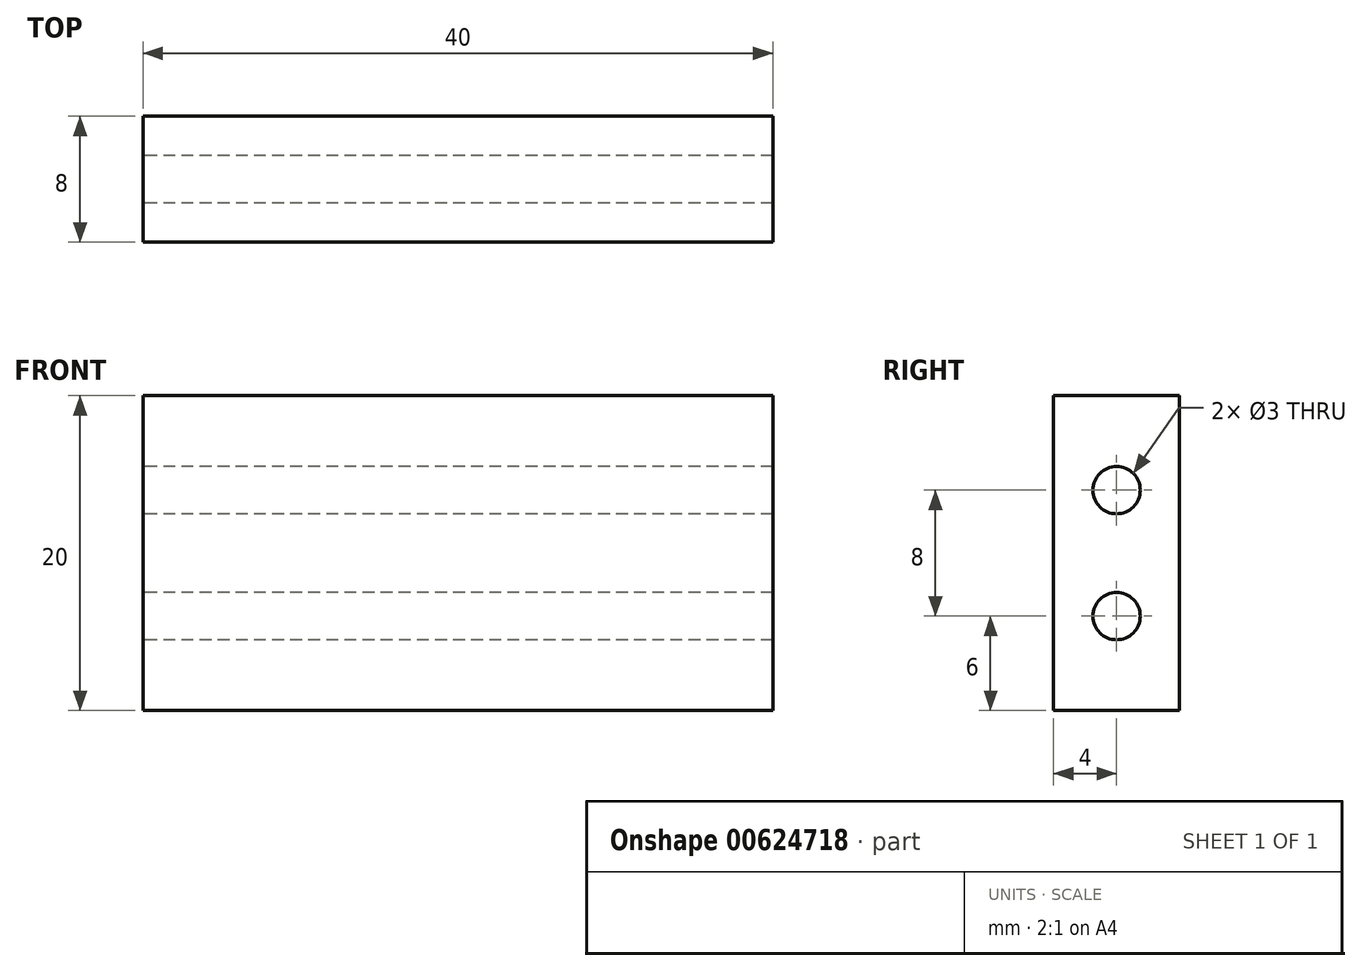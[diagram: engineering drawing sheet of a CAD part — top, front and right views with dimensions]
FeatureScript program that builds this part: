
annotation { "Feature Type Name" : "Feature", "Feature Type Description" : "" }
export const myFeature = defineFeature(function(context is Context, id is Id, definition is map)
    precondition{}
    {
        {
            var Q0;
            Q0=qCreatedBy(makeId("Front.planeOp"),FACE);
            var sketch = newSketch(context, id + "F0", { "sketchPlane" : qUnion([Q0])});
            skLineSegment(sketch, "E0.bottom", {"start": v(-20, -10) * mm, "end": v(20, -10) * mm});
            skLineSegment(sketch, "E0.top", {"start": v(-20, 10) * mm, "end": v(20, 10) * mm});
            skLineSegment(sketch, "E0.left", {"start": v(-20, -10) * mm, "end": v(-20, 10) * mm});
            skLineSegment(sketch, "E0.right", {"start": v(20, -10) * mm, "end": v(20, 10) * mm});
            skPoint(sketch, "E0.middle", {"position": v(0, 0) * mm});
            skSolve(sketch);
        }
        {
            var Q0;
            Q0=makeQuery(id+"F0.imprint","IMPRINT",FACE,{"disambiguationData":[TD([[makeQuery(id+"F0.imprint","IMPRINT",EDGE,{"derivedFrom":sQuery(id+"F0.wireOp",EDGE,"E0.bottom")}),1.0]])]});
            extrude(context, id + "F1", {"entities" : qUnion([Q0]), "depth" : 8 * mm, "offsetDistance" : 25 * mm});
        }
        {
            var Q0;
            Q0=makeQuery(id+"F1.opExtrude","SWEPT_FACE",FACE,{"disambiguationData":[OSD([sQuery(id+"F0.wireOp",EDGE,"E0.left")])]});
            var sketch = newSketch(context, id + "F2", { "sketchPlane" : qUnion([Q0])});
            skLineSegment(sketch, "E1", {"start": v(4, 10) * mm, "end": v(4, -10) * mm, "construction": true});
            skCircle(sketch, "E2", {"center": v(4, 4) * mm, "radius": 1.5 * mm});
            skCircle(sketch, "E3", {"center": v(4, -4) * mm, "radius": 1.5 * mm});
            skLineSegment(sketch, "E4", {"start": v(0, 0) * mm, "end": v(8, 0) * mm, "construction": true});
            skSolve(sketch);
        }
        {
            var Q0;
            Q0=makeQuery(id+"F2.imprint","IMPRINT",FACE,{"disambiguationData":[TD([[makeQuery(id+"F2.imprint","IMPRINT",EDGE,{"derivedFrom":sQuery(id+"F2.wireOp",EDGE,"E2")}),1.0]])]});
            var Q1;
            Q1=makeQuery(id+"F2.imprint","IMPRINT",FACE,{"disambiguationData":[TD([[makeQuery(id+"F2.imprint","IMPRINT",EDGE,{"derivedFrom":sQuery(id+"F2.wireOp",EDGE,"E3")}),1.0]])]});
            extrude(context, id + "F3", {"entities" : qUnion([Q0, Q1]), "operationType" : NewBodyOperationType.REMOVE, "endBound" : BoundingType.THROUGH_ALL, "oppositeDirection" : true, "depth" : 25 * mm, "offsetDistance" : 25 * mm});
        }
    });
